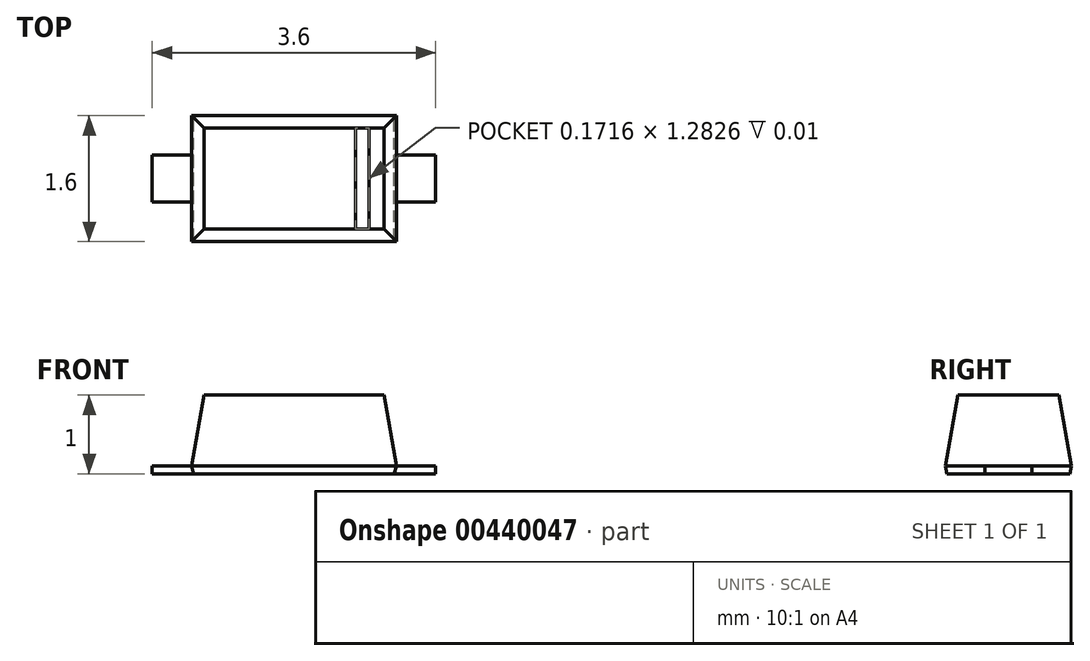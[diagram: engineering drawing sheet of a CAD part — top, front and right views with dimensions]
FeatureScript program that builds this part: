
annotation { "Feature Type Name" : "Feature", "Feature Type Description" : "" }
export const myFeature = defineFeature(function(context is Context, id is Id, definition is map)
    precondition{}
    {
        {
            var Q0;
            Q0=qCreatedBy(makeId("Front.planeOp"),FACE);
            var sketch = newSketch(context, id + "F0", { "sketchPlane" : qUnion([Q0])});
            skLineSegment(sketch, "E0", {"start": v(-1.3, 0) * mm, "end": v(1.3, 0) * mm});
            skLineSegment(sketch, "E1", {"start": v(-1.3, 0) * mm, "end": v(-1.27, -0.1) * mm});
            skLineSegment(sketch, "E2", {"start": v(-1.27, -0.1) * mm, "end": v(1.27, -0.1) * mm});
            skLineSegment(sketch, "E3", {"start": v(1.27, -0.1) * mm, "end": v(1.3, 0) * mm});
            skLineSegment(sketch, "E4", {"start": v(-1.3, 0) * mm, "end": v(-1.14, 0.9) * mm});
            skLineSegment(sketch, "E5", {"start": v(-1.14, 0.9) * mm, "end": v(1.14, 0.9) * mm});
            skLineSegment(sketch, "E6", {"start": v(1.14, 0.9) * mm, "end": v(1.3, 0) * mm});
            skSolve(sketch);
        }
        {
            var Q0;
            Q0 = qSketchRegion(id + "F0", true);
            extrude(context, id + "F1", {"entities" : qUnion([Q0]), "endBound" : BoundingType.SYMMETRIC, "depth" : 1.6 * mm});
        }
        {
            var Q0;
            Q0=qCreatedBy(makeId("Right.planeOp"),FACE);
            var sketch = newSketch(context, id + "F2", { "sketchPlane" : qUnion([Q0])});
            skPoint(sketch, "E7.0", {"position": v(-0.8, 0) * mm});
            skPoint(sketch, "E8.0", {"position": v(0.8, 0) * mm});
            skLineSegment(sketch, "E9.0", {"start": v(-0.8, 0.9) * mm, "end": v(0.8, 0.9) * mm});
            skLineSegment(sketch, "E10.0", {"start": v(-0.8, -0.1) * mm, "end": v(0.8, -0.1) * mm});
            skLineSegment(sketch, "E11", {"start": v(-0.8, 0) * mm, "end": v(-0.64, 0.9) * mm});
            skLineSegment(sketch, "E12", {"start": v(-0.64, 0.9) * mm, "end": v(0.64, 0.9) * mm});
            skLineSegment(sketch, "E13", {"start": v(0.64, 0.9) * mm, "end": v(0.8, 0) * mm});
            skLineSegment(sketch, "E14", {"start": v(0.8, 0) * mm, "end": v(0.78, -0.1) * mm});
            skLineSegment(sketch, "E15", {"start": v(0.78, -0.1) * mm, "end": v(-0.78, -0.1) * mm});
            skLineSegment(sketch, "E16", {"start": v(-0.78, -0.1) * mm, "end": v(-0.8, 0) * mm});
            skLineSegment(sketch, "E17", {"start": v(-0.8, 0) * mm, "end": v(0.8, 0) * mm});
            skLineSegment(sketch, "E18", {"start": v(0.8, 0.9) * mm, "end": v(0.8, 0) * mm});
            skLineSegment(sketch, "E19", {"start": v(0.8, 0) * mm, "end": v(0.8, -0.1) * mm});
            skLineSegment(sketch, "E20", {"start": v(-0.8, -0.1) * mm, "end": v(-0.8, 0) * mm});
            skLineSegment(sketch, "E21", {"start": v(-0.8, 0) * mm, "end": v(-0.8, 0.9) * mm});
            skSolve(sketch);
        }
        {
            var Q0;
            {var subQ2=sQuery(id+"F2.wireOp",EDGE,"E11");Q0=makeQuery(id+"F2.imprint","IMPRINT",FACE,{"disambiguationData":[TD([[makeQuery(id+"F2.imprint","IMPRINT",EDGE,{"derivedFrom":subQ2}),1.0]])]});}
            var Q1;
            {var subQ2=sQuery(id+"F2.wireOp",EDGE,"E13");Q1=makeQuery(id+"F2.imprint","IMPRINT",FACE,{"disambiguationData":[TD([[makeQuery(id+"F2.imprint","IMPRINT",EDGE,{"derivedFrom":subQ2}),1.0]])]});}
            var Q2;
            {var subQ2=sQuery(id+"F2.wireOp",EDGE,"E16");Q2=makeQuery(id+"F2.imprint","IMPRINT",FACE,{"disambiguationData":[TD([[makeQuery(id+"F2.imprint","IMPRINT",EDGE,{"derivedFrom":subQ2}),1.0]])]});}
            var Q3;
            {var subQ2=sQuery(id+"F2.wireOp",EDGE,"E14");Q3=makeQuery(id+"F2.imprint","IMPRINT",FACE,{"disambiguationData":[TD([[makeQuery(id+"F2.imprint","IMPRINT",EDGE,{"derivedFrom":subQ2}),1.0]])]});}
            extrude(context, id + "F3", {"entities" : qUnion([Q0, Q1, Q2, Q3]), "operationType" : NewBodyOperationType.REMOVE, "endBound" : BoundingType.THROUGH_ALL, "oppositeDirection" : true, "depth" : 25 * mm, "hasSecondDirection" : true, "secondDirectionBound" : SecondDirectionBoundingType.THROUGH_ALL, "secondDirectionOppositeDirection" : false, "secondDirectionDepth" : 25 * mm});
        }
        {
            var Q0;
            Q0=qCreatedBy(makeId("Front.planeOp"),FACE);
            var sketch = newSketch(context, id + "F4", { "sketchPlane" : qUnion([Q0])});
            skPoint(sketch, "E22.0", {"position": v(1.3, 0) * mm});
            skPoint(sketch, "E23.0", {"position": v(1.27, -0.1) * mm});
            skPoint(sketch, "E24.0", {"position": v(-1.27, -0.1) * mm});
            skPoint(sketch, "E25.0", {"position": v(-1.3, 0) * mm});
            skLineSegment(sketch, "E26", {"start": v(1.3, 0) * mm, "end": v(1.8, 0) * mm});
            skLineSegment(sketch, "E27", {"start": v(1.8, 0) * mm, "end": v(1.8, -0.1) * mm});
            skLineSegment(sketch, "E28", {"start": v(1.8, -0.1) * mm, "end": v(1.27, -0.1) * mm});
            skLineSegment(sketch, "E29", {"start": v(1.3, 0) * mm, "end": v(1.27, -0.1) * mm});
            skLineSegment(sketch, "E30", {"start": v(-1.3, 0) * mm, "end": v(-1.8, 0) * mm});
            skLineSegment(sketch, "E31", {"start": v(-1.8, 0) * mm, "end": v(-1.8, -0.1) * mm});
            skLineSegment(sketch, "E32", {"start": v(-1.8, -0.1) * mm, "end": v(-1.27, -0.1) * mm});
            skLineSegment(sketch, "E33", {"start": v(-1.27, -0.1) * mm, "end": v(-1.3, 0) * mm});
            skPoint(sketch, "E34.0", {"position": v(0, 0) * mm});
            skLineSegment(sketch, "E35", {"start": v(0, 0) * mm, "end": v(0, -0.27) * mm});
            skSolve(sketch);
        }
        {
            var Q0;
            Q0 = qSketchRegion(id + "F4", true);
            extrude(context, id + "F5", {"entities" : qUnion([Q0]), "endBound" : BoundingType.SYMMETRIC, "depth" : 0.6 * mm});
        }
        {
            var Q0;
            Q0=makeQuery(id+"F1.opExtrude","SWEPT_FACE",FACE,{"disambiguationData":[OSD([sQuery(id+"F0.wireOp",EDGE,"E5")])]});
            var sketch = newSketch(context, id + "F6", { "sketchPlane" : qUnion([Q0])});
            skLineSegment(sketch, "E36.bottom", {"start": v(0.95, -0.64) * mm, "end": v(0.78, -0.64) * mm});
            skLineSegment(sketch, "E36.top", {"start": v(0.95, 0.64) * mm, "end": v(0.78, 0.64) * mm});
            skLineSegment(sketch, "E36.left", {"start": v(0.95, -0.64) * mm, "end": v(0.95, 0.64) * mm});
            skLineSegment(sketch, "E36.right", {"start": v(0.78, -0.64) * mm, "end": v(0.78, 0.64) * mm});
            skSolve(sketch);
        }
        {
            var Q0;
            Q0 = qSketchRegion(id + "F6", true);
            extrude(context, id + "F7", {"entities" : qUnion([Q0]), "operationType" : NewBodyOperationType.REMOVE, "oppositeDirection" : true, "depth" : 0.01 * mm});
        }
    });
